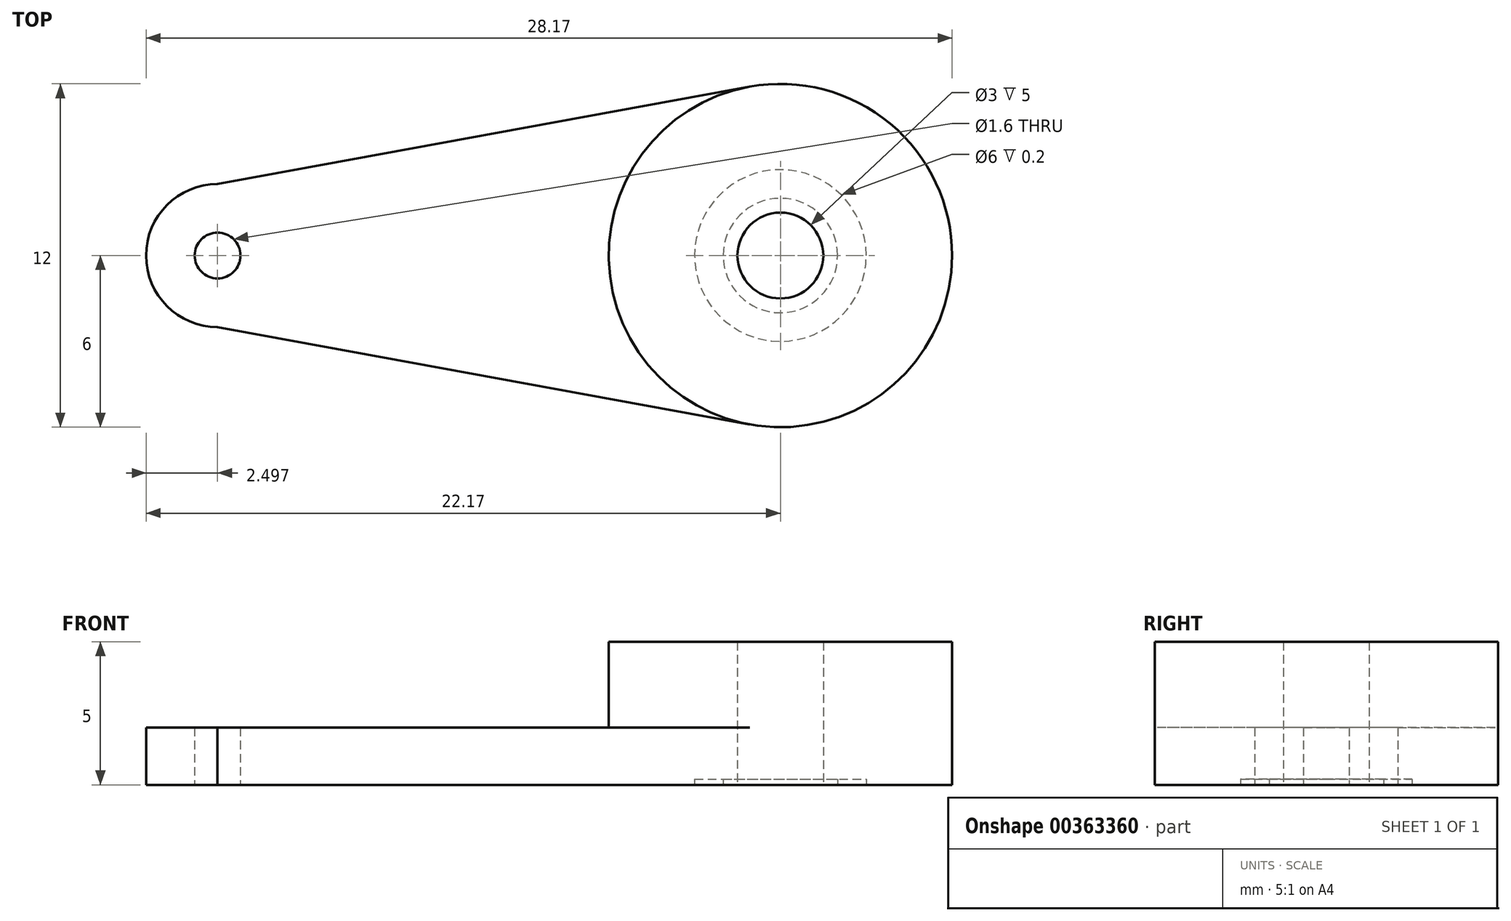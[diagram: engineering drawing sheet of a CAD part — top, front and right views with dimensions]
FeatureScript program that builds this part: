
annotation { "Feature Type Name" : "Feature", "Feature Type Description" : "" }
export const myFeature = defineFeature(function(context is Context, id is Id, definition is map)
    precondition{}
    {
        {
            var Q0;
            Q0=qCreatedBy(makeId("Top.planeOp"),FACE);
            var sketch = newSketch(context, id + "F0", { "sketchPlane" : qUnion([Q0])});
            skCircle(sketch, "E0", {"center": v(0, 0) * mm, "radius": 6 * mm});
            skCircle(sketch, "E1", {"center": v(-19.67, 0) * mm, "radius": 2.5 * mm});
            skLineSegment(sketch, "E2", {"start": v(-19.67, 2.5) * mm, "end": v(0, 6.1) * mm});
            skLineSegment(sketch, "E3", {"start": v(-19.67, -2.5) * mm, "end": v(0, -6.1) * mm});
            skCircle(sketch, "E4", {"center": v(0, 0) * mm, "radius": 1.5 * mm});
            skCircle(sketch, "E5", {"center": v(-19.67, 0) * mm, "radius": 0.8 * mm});
            skSolve(sketch);
        }
        {
            var Q0;
            Q0=makeQuery(id+"F0.imprint","IMPRINT",FACE,{"disambiguationData":[TD([[makeQuery(id+"F0.imprint","IMPRINT",EDGE,{"derivedFrom":sQuery(id+"F0.wireOp",EDGE,"E4")}),-1.0]])]});
            extrude(context, id + "F1", {"entities" : qUnion([Q0]), "depth" : 5 * mm});
        }
        {
            var Q0;
            {var subQ0=sQuery(id+"F0.wireOp",EDGE,"E2");var subQ1=sQuery(id+"F0.wireOp",EDGE,"E0");var subQ2=makeQuery(id+"F0.imprint","INTERSECT",VERTEX,{"derivedFrom":[subQ1,subQ0]});Q0=makeQuery(id+"F0.imprint","IMPRINT",FACE,{"disambiguationData":[TD([[makeQuery(id+"F0.imprint","IMPRINT",EDGE,{"disambiguationData":[TD([[subQ2,-1.0]])],"derivedFrom":subQ1}),-1.0]])]});}
            var Q1;
            Q1=makeQuery(id+"F0.imprint","IMPRINT",FACE,{"disambiguationData":[TD([[makeQuery(id+"F0.imprint","IMPRINT",EDGE,{"derivedFrom":sQuery(id+"F0.wireOp",EDGE,"E5")}),-1.0]])]});
            extrude(context, id + "F2", {"entities" : qUnion([Q0, Q1]), "operationType" : NewBodyOperationType.ADD, "depth" : 2 * mm});
        }
        {
            var Q0;
            {var subQ0=sQuery(id+"F0.wireOp",EDGE,"E0");Q0=makeQuery(id+"F2.boolean.opBoolean","MERGE",FACE,{"derivedFrom":[makeQuery(id+"F1.opExtrude","CAP_FACE",FACE,{"disambiguationData":[OSD([subQ0,sQuery(id+"F0.wireOp",EDGE,"E4")])],"isStart":true}),makeQuery(id+"F2.opExtrude","CAP_FACE",FACE,{"disambiguationData":[OSD([subQ0,sQuery(id+"F0.wireOp",EDGE,"E1"),sQuery(id+"F0.wireOp",EDGE,"E2"),sQuery(id+"F0.wireOp",EDGE,"E3"),sQuery(id+"F0.wireOp",EDGE,"E5")])],"isStart":true})]});}
            var sketch = newSketch(context, id + "F3", { "sketchPlane" : qUnion([Q0])});
            skCircle(sketch, "E6", {"center": v(0, 0) * mm, "radius": 2 * mm});
            skCircle(sketch, "E7", {"center": v(0, 0) * mm, "radius": 3 * mm});
            skSolve(sketch);
        }
        {
            var Q0;
            Q0 = qSketchRegion(id + "F3", true);
            extrude(context, id + "F4", {"entities" : qUnion([Q0]), "operationType" : NewBodyOperationType.REMOVE, "oppositeDirection" : true, "depth" : 0.2 * mm});
        }
    });
